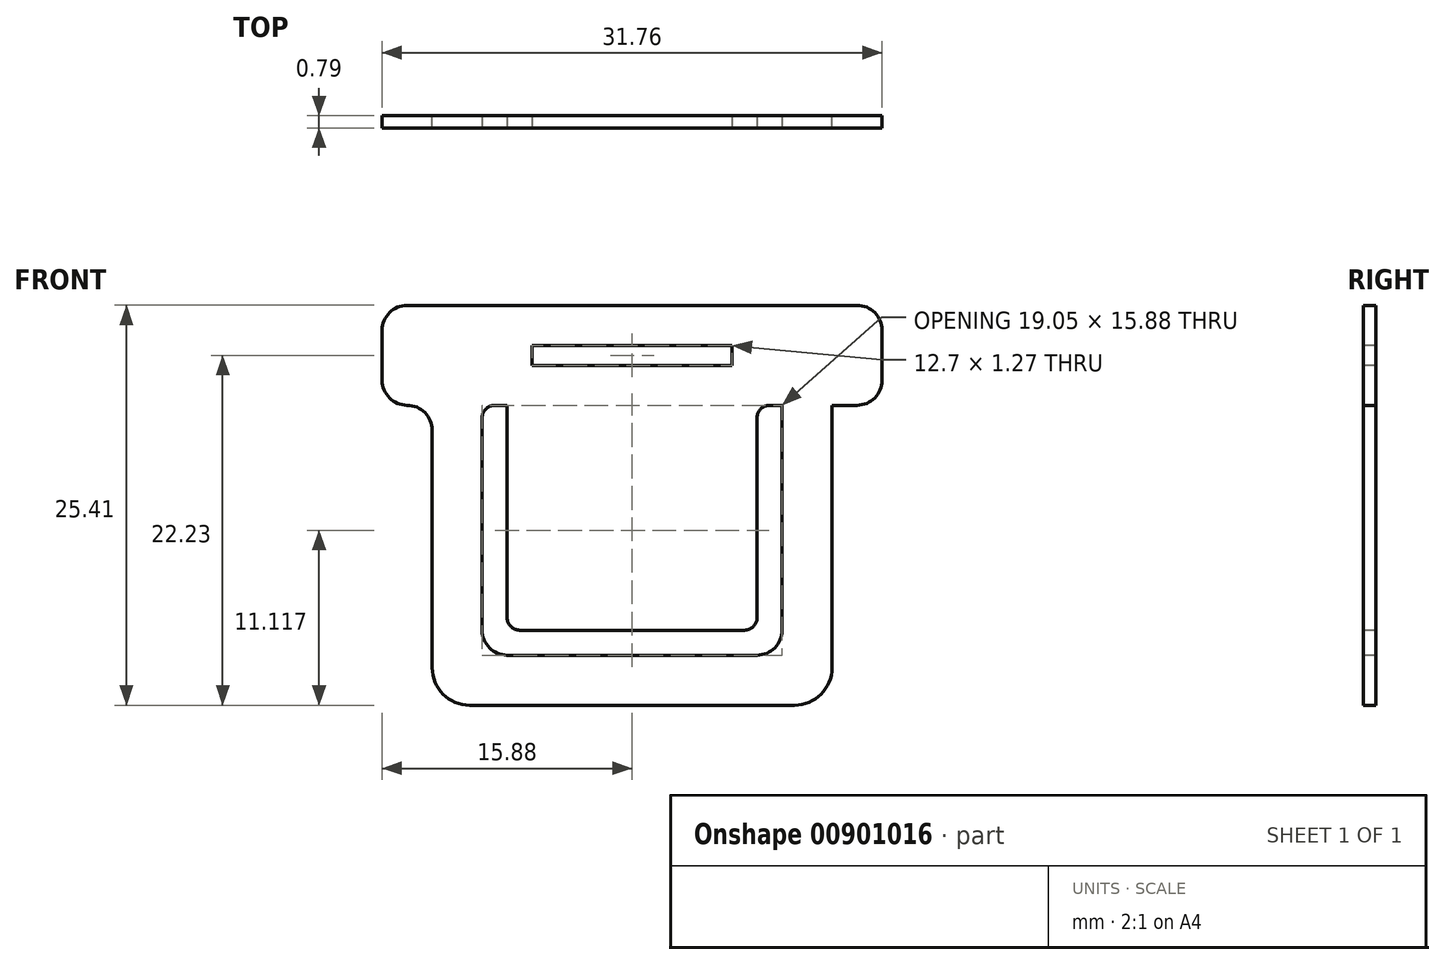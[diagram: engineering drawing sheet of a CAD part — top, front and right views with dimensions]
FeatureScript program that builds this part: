
annotation { "Feature Type Name" : "Feature", "Feature Type Description" : "" }
export const myFeature = defineFeature(function(context is Context, id is Id, definition is map)
    precondition{}
    {
        {
            var Q0;
            Q0=qCreatedBy(makeId("Front.planeOp"),FACE);
            var sketch = newSketch(context, id + "F0", { "sketchPlane" : qUnion([Q0])});
            skLineSegment(sketch, "E0.bottom", {"start": v(12.7, 9.53) * mm, "end": v(-12.7, 9.53) * mm});
            skLineSegment(sketch, "E0.top", {"start": v(12.7, -9.53) * mm, "end": v(-12.7, -9.53) * mm});
            skLineSegment(sketch, "E0.left", {"start": v(12.7, 9.53) * mm, "end": v(12.7, -9.53) * mm});
            skLineSegment(sketch, "E0.right", {"start": v(-12.7, 9.53) * mm, "end": v(-12.7, -9.53) * mm});
            skPoint(sketch, "E0.middle", {"position": v(0, 0) * mm});
            skSolve(sketch);
        }
        {
            var Q0;
            Q0=makeQuery(id+"F0.imprint","IMPRINT",FACE,{"disambiguationData":[TD([[makeQuery(id+"F0.imprint","IMPRINT",EDGE,{"derivedFrom":sQuery(id+"F0.wireOp",EDGE,"E0.bottom")}),1.0]])]});
            extrude(context, id + "F1", {"entities" : qUnion([Q0]), "depth" : 0.8 * mm, "offsetDistance" : 25.4 * mm});
        }
        {
            var Q0;
            Q0=makeQuery(id+"F1.opExtrude","SWEPT_EDGE",EDGE,{"disambiguationData":[OSD([sQuery(id+"F0.wireOp",EDGE,"E0.top"),sQuery(id+"F0.wireOp",EDGE,"E0.left")])]});
            var Q1;
            Q1=makeQuery(id+"F1.opExtrude","SWEPT_EDGE",EDGE,{"disambiguationData":[OSD([sQuery(id+"F0.wireOp",EDGE,"E0.top"),sQuery(id+"F0.wireOp",EDGE,"E0.right")])]});
            fillet(context, id + "F2", {"entities" : qUnion([Q0, Q1]), "radius" : 2.38 * mm, "tangentPropagation" : true, "allowEdgeOverflow" : false});
        }
        {
            var Q0;
            Q0=makeQuery(id+"F1.opExtrude","CAP_FACE",FACE,{"disambiguationData":[OSD([sQuery(id+"F0.wireOp",EDGE,"E0.bottom"),sQuery(id+"F0.wireOp",EDGE,"E0.top"),sQuery(id+"F0.wireOp",EDGE,"E0.left"),sQuery(id+"F0.wireOp",EDGE,"E0.right")])],"isStart":false});
            var sketch = newSketch(context, id + "F3", { "sketchPlane" : qUnion([Q0])});
            skLineSegment(sketch, "E1.bottom", {"start": v(9.52, 9.53) * mm, "end": v(-9.53, 9.53) * mm});
            skLineSegment(sketch, "E1.top", {"start": v(9.53, -6.35) * mm, "end": v(-9.53, -6.35) * mm});
            skLineSegment(sketch, "E1.left", {"start": v(9.52, 9.53) * mm, "end": v(9.53, -6.35) * mm});
            skLineSegment(sketch, "E1.right", {"start": v(-9.53, 9.53) * mm, "end": v(-9.52, -6.35) * mm});
            skPoint(sketch, "E1.middle", {"position": v(0, 0) * mm});
            skSolve(sketch);
        }
        {
            var Q0;
            Q0=makeQuery(id+"F3.imprint","IMPRINT",FACE,{"disambiguationData":[TD([[makeQuery(id+"F3.imprint","IMPRINT",EDGE,{"derivedFrom":sQuery(id+"F3.wireOp",EDGE,"E1.bottom")}),1.0]])]});
            extrude(context, id + "F4", {"entities" : qUnion([Q0]), "operationType" : NewBodyOperationType.REMOVE, "oppositeDirection" : true, "depth" : 4.93 * mm, "offsetDistance" : 25.4 * mm});
        }
        {
            var Q0;
            Q0=makeQuery(id+"F1.opExtrude","CAP_FACE",FACE,{"disambiguationData":[OSD([sQuery(id+"F0.wireOp",EDGE,"E0.bottom"),sQuery(id+"F0.wireOp",EDGE,"E0.top"),sQuery(id+"F0.wireOp",EDGE,"E0.left"),sQuery(id+"F0.wireOp",EDGE,"E0.right")])],"isStart":false});
            var sketch = newSketch(context, id + "F5", { "sketchPlane" : qUnion([Q0])});
            skLineSegment(sketch, "E2.bottom", {"start": v(-15.88, 9.53) * mm, "end": v(15.87, 9.53) * mm});
            skLineSegment(sketch, "E2.top", {"start": v(-15.88, 15.87) * mm, "end": v(15.87, 15.88) * mm});
            skLineSegment(sketch, "E2.left", {"start": v(-15.88, 9.53) * mm, "end": v(-15.88, 15.87) * mm});
            skLineSegment(sketch, "E2.right", {"start": v(15.87, 9.53) * mm, "end": v(15.87, 15.88) * mm});
            skLineSegment(sketch, "E3.bottom", {"start": v(-6.35, 13.34) * mm, "end": v(6.35, 13.34) * mm});
            skLineSegment(sketch, "E3.top", {"start": v(-6.35, 12.07) * mm, "end": v(6.35, 12.07) * mm});
            skLineSegment(sketch, "E3.left", {"start": v(-6.35, 13.34) * mm, "end": v(-6.35, 12.07) * mm});
            skLineSegment(sketch, "E3.right", {"start": v(6.35, 13.34) * mm, "end": v(6.35, 12.07) * mm});
            skSolve(sketch);
        }
        {
            var Q0;
            Q0=makeQuery(id+"F5.imprint","IMPRINT",FACE,{"disambiguationData":[TD([[makeQuery(id+"F5.imprint","IMPRINT",EDGE,{"derivedFrom":sQuery(id+"F5.wireOp",EDGE,"E2.top")}),-1.0]])]});
            extrude(context, id + "F6", {"entities" : qUnion([Q0]), "operationType" : NewBodyOperationType.ADD, "oppositeDirection" : true, "depth" : 0.8 * mm, "offsetDistance" : 25.4 * mm});
        }
        {
            var Q0;
            Q0=makeQuery(id+"F6.opExtrude","SWEPT_EDGE",EDGE,{"disambiguationData":[OSD([sQuery(id+"F5.wireOp",EDGE,"E2.top"),sQuery(id+"F5.wireOp",EDGE,"E2.left")])]});
            var Q1;
            Q1=makeQuery(id+"F6.opExtrude","SWEPT_EDGE",EDGE,{"disambiguationData":[OSD([sQuery(id+"F5.wireOp",EDGE,"E2.top"),sQuery(id+"F5.wireOp",EDGE,"E2.right")])]});
            var Q2;
            Q2=makeQuery(id+"F6.opExtrude","SWEPT_EDGE",EDGE,{"disambiguationData":[OSD([sQuery(id+"F5.wireOp",EDGE,"E2.bottom"),sQuery(id+"F5.wireOp",EDGE,"E2.right")])]});
            var Q3;
            Q3=makeQuery(id+"F1.opExtrude","SWEPT_EDGE",EDGE,{"disambiguationData":[OSD([sQuery(id+"F0.wireOp",EDGE,"E0.bottom"),sQuery(id+"F0.wireOp",EDGE,"E0.left")])]});
            var Q4;
            Q4=makeQuery(id+"F6.opExtrude","SWEPT_EDGE",EDGE,{"disambiguationData":[OSD([sQuery(id+"F5.wireOp",EDGE,"E2.bottom"),sQuery(id+"F5.wireOp",EDGE,"E2.left")])]});
            var Q5;
            Q5=makeQuery(id+"F1.opExtrude","SWEPT_EDGE",EDGE,{"disambiguationData":[OSD([sQuery(id+"F0.wireOp",EDGE,"E0.bottom"),sQuery(id+"F0.wireOp",EDGE,"E0.right")])]});
            fillet(context, id + "F7", {"entities" : qUnion([Q0, Q1, Q2, Q3, Q4, Q5]), "radius" : 1.59 * mm, "tangentPropagation" : true, "allowEdgeOverflow" : false});
        }
        {
            var Q0;
            Q0=makeQuery(id+"F4.boolean.opBoolean","COPY",EDGE,{"derivedFrom":makeQuery(id+"F4.opExtrude","SWEPT_EDGE",EDGE,{"disambiguationData":[OSD([sQuery(id+"F3.wireOp",EDGE,"E1.top"),sQuery(id+"F3.wireOp",EDGE,"E1.right")])]})});
            var Q1;
            Q1=makeQuery(id+"F4.boolean.opBoolean","COPY",EDGE,{"derivedFrom":makeQuery(id+"F4.opExtrude","SWEPT_EDGE",EDGE,{"disambiguationData":[OSD([sQuery(id+"F3.wireOp",EDGE,"E1.top"),sQuery(id+"F3.wireOp",EDGE,"E1.left")])]})});
            fillet(context, id + "F8", {"entities" : qUnion([Q0, Q1]), "radius" : 1.59 * mm, "tangentPropagation" : true, "allowEdgeOverflow" : false});
        }
        {
            var Q0;
            Q0=makeQuery(id+"F6.boolean.opBoolean","MERGE",FACE,{"derivedFrom":[makeQuery(id+"F1.opExtrude","CAP_FACE",FACE,{"disambiguationData":[OSD([sQuery(id+"F0.wireOp",EDGE,"E0.bottom"),sQuery(id+"F0.wireOp",EDGE,"E0.top"),sQuery(id+"F0.wireOp",EDGE,"E0.left"),sQuery(id+"F0.wireOp",EDGE,"E0.right")])],"isStart":false}),makeQuery(id+"F6.opExtrude","CAP_FACE",FACE,{"disambiguationData":[OSD([sQuery(id+"F5.wireOp",EDGE,"E2.bottom"),sQuery(id+"F5.wireOp",EDGE,"E2.top"),sQuery(id+"F5.wireOp",EDGE,"E2.left"),sQuery(id+"F5.wireOp",EDGE,"E2.right")])],"isStart":true})]});
            var sketch = newSketch(context, id + "F9", { "sketchPlane" : qUnion([Q0])});
            skLineSegment(sketch, "E4.bottom", {"start": v(-7.94, 9.53) * mm, "end": v(7.94, 9.53) * mm});
            skLineSegment(sketch, "E4.top", {"start": v(-7.94, -4.76) * mm, "end": v(7.94, -4.76) * mm});
            skLineSegment(sketch, "E4.left", {"start": v(-7.94, 9.53) * mm, "end": v(-7.94, -4.76) * mm});
            skLineSegment(sketch, "E4.right", {"start": v(7.94, 9.53) * mm, "end": v(7.94, -4.76) * mm});
            skSolve(sketch);
        }
        {
            var Q0;
            Q0=makeQuery(id+"F9.imprint","IMPRINT",FACE,{"disambiguationData":[TD([[makeQuery(id+"F9.imprint","IMPRINT",EDGE,{"derivedFrom":sQuery(id+"F9.wireOp",EDGE,"E4.bottom")}),1.0]])]});
            extrude(context, id + "F10", {"entities" : qUnion([Q0]), "operationType" : NewBodyOperationType.ADD, "oppositeDirection" : true, "depth" : 0.8 * mm, "offsetDistance" : 25.4 * mm});
        }
        {
            var Q0;
            Q0=makeQuery(id+"F10.opExtrude","SWEPT_EDGE",EDGE,{"disambiguationData":[OSD([sQuery(id+"F5.wireOp",EDGE,"E2.bottom"),sQuery(id+"F9.wireOp",EDGE,"E4.bottom"),sQuery(id+"F9.wireOp",EDGE,"E4.left")])]});
            var Q1;
            Q1=makeQuery(id+"F4.boolean.opBoolean","COPY",EDGE,{"derivedFrom":makeQuery(id+"F4.opExtrude","SWEPT_EDGE",EDGE,{"disambiguationData":[OSD([sQuery(id+"F0.wireOp",EDGE,"E0.bottom"),sQuery(id+"F3.wireOp",EDGE,"E1.bottom"),sQuery(id+"F3.wireOp",EDGE,"E1.right")])]})});
            var Q2;
            Q2=makeQuery(id+"F10.opExtrude","SWEPT_EDGE",EDGE,{"disambiguationData":[OSD([sQuery(id+"F5.wireOp",EDGE,"E2.bottom"),sQuery(id+"F9.wireOp",EDGE,"E4.bottom"),sQuery(id+"F9.wireOp",EDGE,"E4.right")])]});
            var Q3;
            Q3=makeQuery(id+"F4.boolean.opBoolean","COPY",EDGE,{"derivedFrom":makeQuery(id+"F4.opExtrude","SWEPT_EDGE",EDGE,{"disambiguationData":[OSD([sQuery(id+"F0.wireOp",EDGE,"E0.bottom"),sQuery(id+"F3.wireOp",EDGE,"E1.bottom"),sQuery(id+"F3.wireOp",EDGE,"E1.left")])]})});
            fillet(context, id + "F11", {"entities" : qUnion([Q0, Q1, Q2, Q3]), "radius" : 0.8 * mm, "tangentPropagation" : true, "allowEdgeOverflow" : false});
        }
        {
            var Q0;
            Q0=makeQuery(id+"F10.opExtrude","SWEPT_EDGE",EDGE,{"disambiguationData":[OSD([sQuery(id+"F9.wireOp",EDGE,"E4.top"),sQuery(id+"F9.wireOp",EDGE,"E4.left")])]});
            var Q1;
            Q1=makeQuery(id+"F10.opExtrude","SWEPT_EDGE",EDGE,{"disambiguationData":[OSD([sQuery(id+"F9.wireOp",EDGE,"E4.top"),sQuery(id+"F9.wireOp",EDGE,"E4.right")])]});
            fillet(context, id + "F12", {"entities" : qUnion([Q0, Q1]), "radius" : 0.8 * mm, "tangentPropagation" : true, "allowEdgeOverflow" : false});
        }
    });
